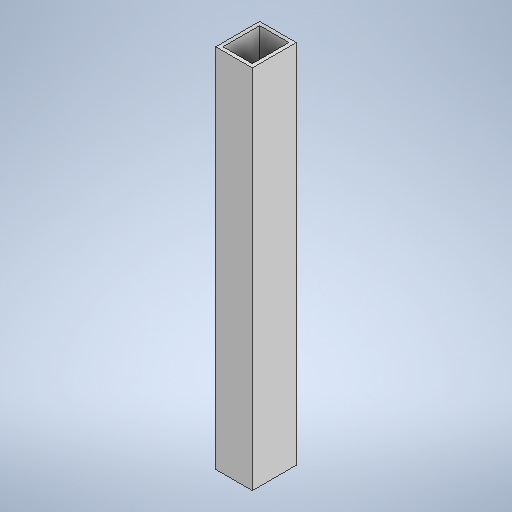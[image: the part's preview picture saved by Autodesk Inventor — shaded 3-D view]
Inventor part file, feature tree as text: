
AUTODESK INVENTOR PART (.ipt)
format: ipt  version: 2025 (Build 290162000, 162)  size: 257,024 bytes
history: native  units: in
note: dims shown in document units (in); Inventor stores cm internally (conversion verified against a paired STEP export)
features: extrude x2, sketch x2
ambient origin geometry x8: Origin, YZ Plane, XZ Plane, XY Plane, X Axis, Y Axis, Z Axis, Center Point
bodies: Solid1 (feature_tree)
feature tree (4):
  extrude  "Extrusion1"  Depth=0.9843in
  extrude  "Extrusion2"  Depth=0.9843in
  sketch  "Sketch1"  dims[d0=1.1811in d1=0.9843in]
  sketch  "Sketch2"  dims[d2=9.8425in d3=0.0in d4=0.9843in d5=0.7874in d6=23.622in d7=0.0in]
